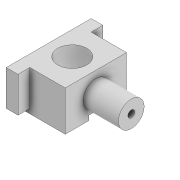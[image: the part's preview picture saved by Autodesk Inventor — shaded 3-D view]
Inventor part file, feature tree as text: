
AUTODESK INVENTOR PART (.ipt)
format: ipt  version: 2022 (Build 260153000, 153)  size: 165,376 bytes
history: native  units: mm
features: extrude x6, sketch x6, projected_geometry x1
ambient origin geometry x8: Origin, YZ Plane, XZ Plane, XY Plane, X Axis, Y Axis, Z Axis, Center Point
bodies: Solid1 (feature_tree)
feature tree (13):
  extrude  "Extrusion1"  Depth=10.0mm
  extrude  "Extrusion2"  Depth=10.0mm
  sketch  "Sketch3"  dims[d4=13.0mm d5=15.0mm d6=0.0mm]
  extrude  "Extrusion3"  Depth=15.0mm TaperAngle=0.0deg
  extrude  "Extrusion6"  Depth=6.5mm
  extrude  "Extrusion7"  Depth=55.0mm TaperAngle=0.0deg
  extrude  "Extrusion8"  Depth=15.0mm TaperAngle=0.0deg
  sketch  "Sketch1"  dims[d0=12.3mm d1=10.0mm]
  sketch  "Sketch2"  dims[d2=10.0mm d3=13.0mm]
  projected_geometry  "Projected Loop1"
  sketch  "Sketch6"  dims[d7=2.9mm d8=6.5mm]
  sketch  "Sketch7"  dims[d11=13.0mm d13=55.0mm d14=0.0mm]
  sketch  "Sketch8"  dims[d16=4.0mm d17=15.0mm d18=0.0mm d21=3.2mm d22=3.2mm d23=4.0mm d24=4.0mm d31=5.0mm d32=5.0mm d33=0.0mm d34=5.0mm d35=5.0mm d36=0.0mm d37=10.0mm d38=10.0mm d39=2.0mm d40=0.0mm]
